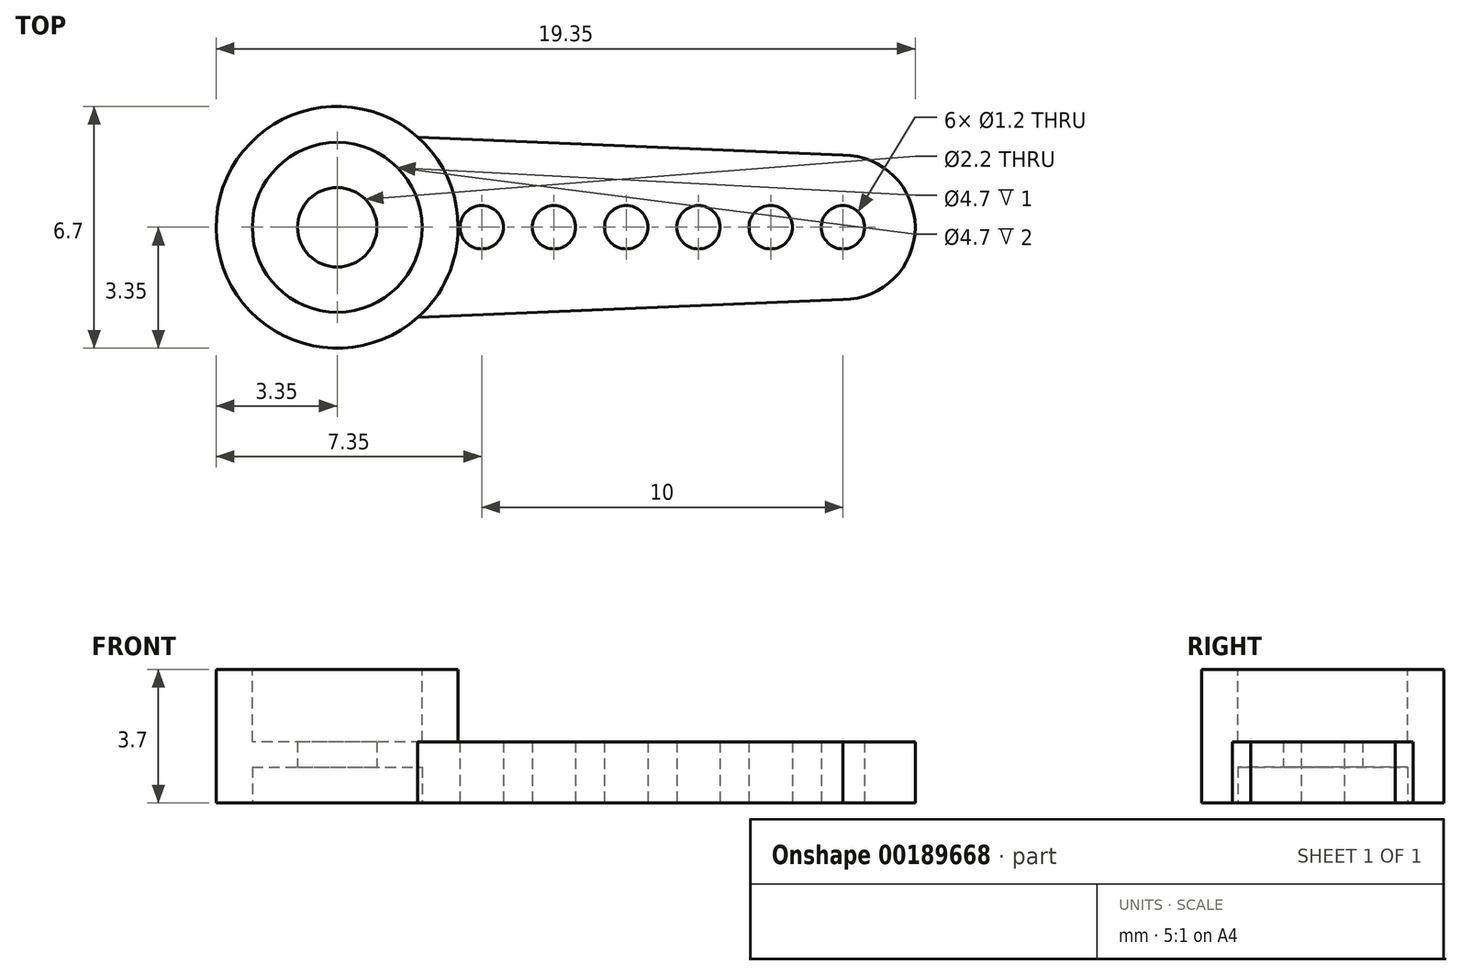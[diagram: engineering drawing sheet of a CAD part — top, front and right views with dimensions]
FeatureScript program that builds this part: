
annotation { "Feature Type Name" : "Feature", "Feature Type Description" : "" }
export const myFeature = defineFeature(function(context is Context, id is Id, definition is map)
    precondition{}
    {
        {
            var Q0;
            Q0=qCreatedBy(makeId("Top.planeOp"),FACE);
            var sketch = newSketch(context, id + "F0", { "sketchPlane" : qUnion([Q0])});
            skCircle(sketch, "E0", {"center": v(0, 0) * mm, "radius": 3.35 * mm});
            skCircle(sketch, "E1", {"center": v(6, 0) * mm, "radius": 0.6 * mm});
            skCircle(sketch, "E2.1.0.0", {"center": v(8, 0) * mm, "radius": 0.6 * mm});
            skCircle(sketch, "E2.2.0.0", {"center": v(10, 0) * mm, "radius": 0.6 * mm});
            skCircle(sketch, "E2.3.0.0", {"center": v(12, 0) * mm, "radius": 0.6 * mm});
            skCircle(sketch, "E2.4.0.0", {"center": v(14, 0) * mm, "radius": 0.6 * mm});
            skLineSegment(sketch, "E2.direction1", {"start": v(6, 0) * mm, "end": v(8, 0) * mm, "construction": true});
            skCircle(sketch, "E3.1.0.0", {"center": v(4, 0) * mm, "radius": 0.6 * mm});
            skLineSegment(sketch, "E3.direction1", {"start": v(6, 0) * mm, "end": v(4, 0) * mm, "construction": true});
            skLineSegment(sketch, "E4", {"start": v(2.23, 2.5) * mm, "end": v(14, 2) * mm});
            skLineSegment(sketch, "E5", {"start": v(0, 0) * mm, "end": v(1.18, 0) * mm, "construction": true});
            skLineSegment(sketch, "E6", {"start": v(2.23, -2.5) * mm, "end": v(14, -2) * mm});
            skArc(sketch, "E7", {"start": v(14, 2) * mm, "mid": v(16, 0) * mm, "end": v(14, -2) * mm});
            skSolve(sketch);
        }
        {
            var Q0;
            {var subQ0=sQuery(id+"F0.wireOp",EDGE,"E0");var subQ1=makeQuery(id+"F0.imprint","INTERSECT",VERTEX,{"derivedFrom":[subQ0,sQuery(id+"F0.wireOp",EDGE,"E4")]});Q0=makeQuery(id+"F0.imprint","IMPRINT",FACE,{"disambiguationData":[TD([[makeQuery(id+"F0.imprint","IMPRINT",EDGE,{"disambiguationData":[TD([[subQ1,-1.0]])],"derivedFrom":subQ0}),1.0]])]});}
            var Q1;
            Q1=makeQuery(id+"F0.imprint","IMPRINT",FACE,{"disambiguationData":[TD([[makeQuery(id+"F0.imprint","IMPRINT",EDGE,{"derivedFrom":sQuery(id+"F0.wireOp",EDGE,"E1")}),-1.0]])]});
            extrude(context, id + "F1", {"entities" : qUnion([Q0, Q1]), "depth" : 1.7 * mm});
        }
        {
            var Q0;
            Q0=makeQuery(id+"F1.opExtrude","CAP_FACE",FACE,{"disambiguationData":[OSD([sQuery(id+"F0.wireOp",EDGE,"E0"),sQuery(id+"F0.wireOp",EDGE,"E1"),sQuery(id+"F0.wireOp",EDGE,"E2.1.0.0"),sQuery(id+"F0.wireOp",EDGE,"E2.2.0.0"),sQuery(id+"F0.wireOp",EDGE,"E2.3.0.0"),sQuery(id+"F0.wireOp",EDGE,"E2.4.0.0"),sQuery(id+"F0.wireOp",EDGE,"E3.1.0.0"),sQuery(id+"F0.wireOp",EDGE,"E4"),sQuery(id+"F0.wireOp",EDGE,"E6"),sQuery(id+"F0.wireOp",EDGE,"4d52fdd3-3aff-440c-9459-d1f9478f26ee")])],"isStart":false});
            var sketch = newSketch(context, id + "F2", { "sketchPlane" : qUnion([Q0])});
            skArc(sketch, "E8.0", {"start": v(2.23, 2.5) * mm, "mid": v(-3.35, 0) * mm, "end": v(2.23, -2.5) * mm});
            skArc(sketch, "E9", {"start": v(2.23, 2.5) * mm, "mid": v(3.35, 0) * mm, "end": v(2.23, -2.5) * mm});
            skSolve(sketch);
        }
        {
            var Q0;
            Q0=makeQuery(id+"F2.imprint","IMPRINT",FACE,{"disambiguationData":[TD([[makeQuery(id+"F2.imprint","IMPRINT",EDGE,{"derivedFrom":sQuery(id+"F2.wireOp",EDGE,"E8.0")}),1.0]])]});
            extrude(context, id + "F3", {"entities" : qUnion([Q0]), "operationType" : NewBodyOperationType.ADD, "depth" : 2 * mm});
        }
        {
            var Q0;
            Q0=makeQuery(id+"F1.opExtrude","CAP_FACE",FACE,{"disambiguationData":[OSD([sQuery(id+"F0.wireOp",EDGE,"E0"),sQuery(id+"F0.wireOp",EDGE,"E1"),sQuery(id+"F0.wireOp",EDGE,"E2.1.0.0"),sQuery(id+"F0.wireOp",EDGE,"E2.2.0.0"),sQuery(id+"F0.wireOp",EDGE,"E2.3.0.0"),sQuery(id+"F0.wireOp",EDGE,"E2.4.0.0"),sQuery(id+"F0.wireOp",EDGE,"E3.1.0.0"),sQuery(id+"F0.wireOp",EDGE,"E4"),sQuery(id+"F0.wireOp",EDGE,"E6"),sQuery(id+"F0.wireOp",EDGE,"4d52fdd3-3aff-440c-9459-d1f9478f26ee")])],"isStart":true});
            var sketch = newSketch(context, id + "F4", { "sketchPlane" : qUnion([Q0])});
            skArc(sketch, "E10.0", {"start": v(2.23, -2.5) * mm, "mid": v(-3.35, 0) * mm, "end": v(2.23, 2.5) * mm, "construction": true});
            skArc(sketch, "E11.0", {"start": v(1.56, -1.75) * mm, "mid": v(-2.35, 0) * mm, "end": v(1.56, 1.75) * mm});
            skArc(sketch, "E12", {"start": v(1.56, -1.75) * mm, "mid": v(2.35, 0) * mm, "end": v(1.56, 1.75) * mm});
            skSolve(sketch);
        }
        {
            var Q0;
            Q0 = qSketchRegion(id + "F4", true);
            extrude(context, id + "F5", {"entities" : qUnion([Q0]), "operationType" : NewBodyOperationType.REMOVE, "oppositeDirection" : true, "depth" : 1 * mm});
        }
        {
            var Q0;
            Q0=makeQuery(id+"F5.boolean.opBoolean","COPY",FACE,{"derivedFrom":makeQuery(id+"F5.opExtrude","CAP_FACE",FACE,{"disambiguationData":[OSD([sQuery(id+"F4.wireOp",EDGE,"E11.0"),sQuery(id+"F4.wireOp",EDGE,"E12")])],"isStart":false})});
            var sketch = newSketch(context, id + "F6", { "sketchPlane" : qUnion([Q0])});
            skCircle(sketch, "E13", {"center": v(0, 0) * mm, "radius": 1.1 * mm});
            skSolve(sketch);
        }
        {
            var Q0;
            Q0=makeQuery(id+"F6.imprint","IMPRINT",FACE,{"disambiguationData":[TD([[makeQuery(id+"F6.imprint","IMPRINT",EDGE,{"derivedFrom":sQuery(id+"F6.wireOp",EDGE,"E13")}),1.0]])]});
            extrude(context, id + "F7", {"entities" : qUnion([Q0]), "operationType" : NewBodyOperationType.REMOVE, "endBound" : BoundingType.THROUGH_ALL, "oppositeDirection" : true, "depth" : 25 * mm});
        }
        {
            var Q0;
            Q0=makeQuery(id+"F3.opExtrude","CAP_FACE",FACE,{"disambiguationData":[OSD([sQuery(id+"F2.wireOp",EDGE,"E8.0"),sQuery(id+"F2.wireOp",EDGE,"E9")])],"isStart":false});
            var sketch = newSketch(context, id + "F8", { "sketchPlane" : qUnion([Q0])});
            skCircle(sketch, "E14.0", {"center": v(0, 0) * mm, "radius": 3.35 * mm, "construction": true});
            skCircle(sketch, "E15.0", {"center": v(0, 0) * mm, "radius": 2.35 * mm});
            skSolve(sketch);
        }
        {
            var Q0;
            Q0 = qSketchRegion(id + "F8", true);
            var Q1;
            Q1=makeQuery(id+"F1.opExtrude","CAP_FACE",FACE,{"disambiguationData":[OSD([sQuery(id+"F0.wireOp",EDGE,"E0"),sQuery(id+"F0.wireOp",EDGE,"E1"),sQuery(id+"F0.wireOp",EDGE,"E2.1.0.0"),sQuery(id+"F0.wireOp",EDGE,"E2.2.0.0"),sQuery(id+"F0.wireOp",EDGE,"E2.3.0.0"),sQuery(id+"F0.wireOp",EDGE,"E2.4.0.0"),sQuery(id+"F0.wireOp",EDGE,"E3.1.0.0"),sQuery(id+"F0.wireOp",EDGE,"E4"),sQuery(id+"F0.wireOp",EDGE,"E6"),sQuery(id+"F0.wireOp",EDGE,"4d52fdd3-3aff-440c-9459-d1f9478f26ee")])],"isStart":false});
            extrude(context, id + "F9", {"entities" : qUnion([Q0]), "operationType" : NewBodyOperationType.REMOVE, "endBound" : BoundingType.UP_TO_SURFACE, "oppositeDirection" : true, "endBoundEntityFace" : qUnion([Q1]), "depth" : 25 * mm});
        }
    });
